# Revit family: Zumtobel RESCLITE PRO MRCR mini
name_source: partatom
category: Lighting Fixtures
revit_build: Autodesk Revit 2016 (Build: 20150220_1215(x64)
units: mm (PartAtom-declared; Revit-internal decimal feet)

## family parameters
Cut with Voids When Loaded = No
Host = Face
Light Source = Yes
OmniClass Number = 23.80.70.11
OmniClass Title = Luminaries for Internal Lighting
Part Type = Normal
Room Calculation Point = No
Round Connector Dimension = Use Diameter
Shared = No

## types (4) — shared parameters
Apparent Load = 5 VA
Assembly Code = D5020200
Body = Zumtobel_Metal_White
Color Filter = 16777215
Description = LED Safety luminaire
Dimming Lamp Color Temperature Shift = <None>
Height = 3 mm  [stored 0.00984252 ft]
Lamp = LED
Length = 50 mm  [stored 0.164042 ft]
Manufacturer = Zumtobel Lighting
Tilt Angle = 180.00°
URL = http://www.zumtobel.com
Voltage = 230 V
Width = 50 mm  [stored 0.164042 ft]
zero-valued in all types: Default Elevation

## per-type parameters (varying)
| type | MSC | MSC ESC | Model | Photometric Web File |
| RESCLITE PRO MRCR MINI ANT | Yes | No | 42185664 | 42185664_(STD_LEO).IES |
| RESCLITE PRO MRCR MINI SPOT | No | Yes | 42185667 | 42185667_(STD_LEO).IES |
| RESCLITE PRO MRCR MINI ESC90 | No | Yes | 42185666 | 42185666_(STD_LEO).IES |
| RESCLITE PRO MRCR MINI ESC | No | Yes | 42185665 | 42185665_(STD_LEO).IES |

note: [stored X ft] marks values corroborated as IEEE doubles in the binary element streams (Revit-internal decimal feet)

## geometry (parser evidence)
native form markers: Sweep x3
no freeform markers — native parametric forms only
